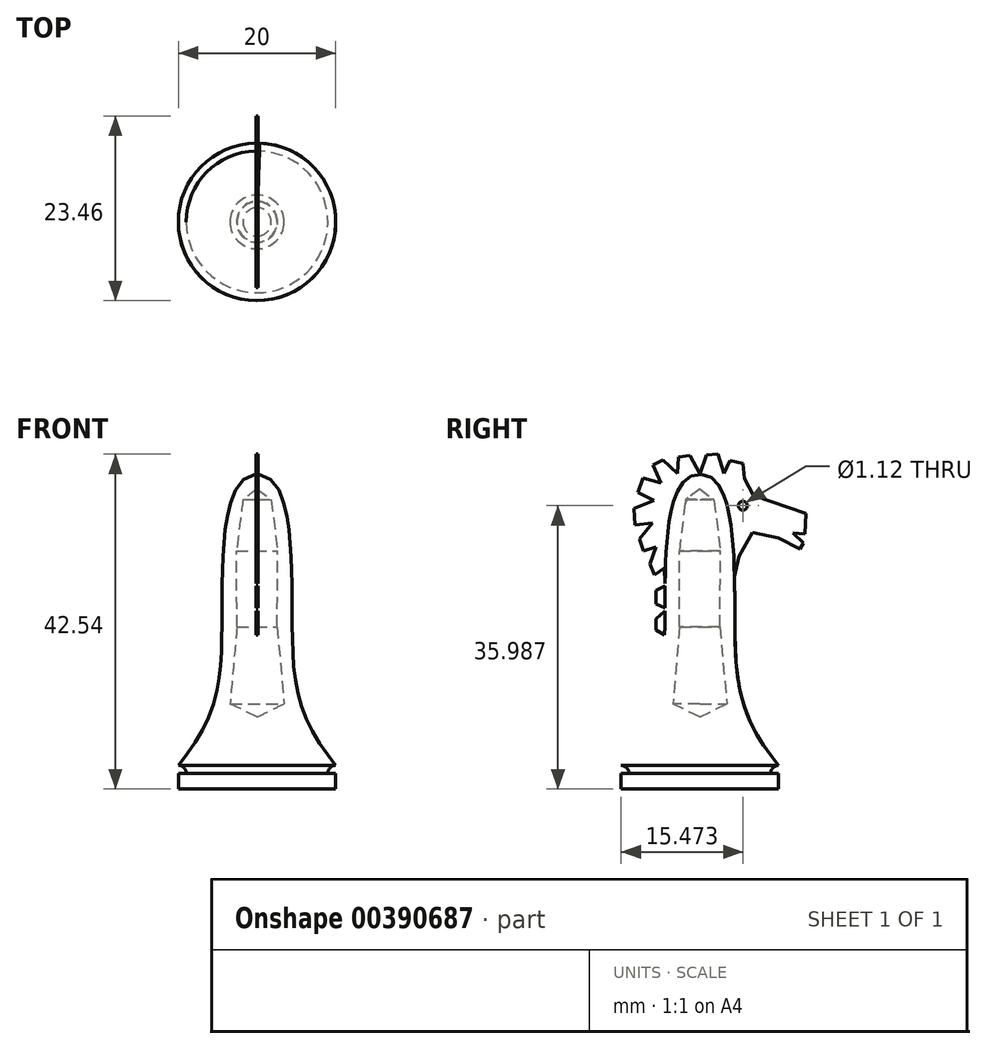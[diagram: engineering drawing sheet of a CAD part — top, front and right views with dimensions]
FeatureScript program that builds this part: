
annotation { "Feature Type Name" : "Feature", "Feature Type Description" : "" }
export const myFeature = defineFeature(function(context is Context, id is Id, definition is map)
    precondition{}
    {
        {
            assignVariable(context, id + "F0", {"name" : "r", "anyValue" : 1});
        }
        {
            var Q0;
            Q0=qCreatedBy(makeId("Front.planeOp"),FACE);
            var sketch = newSketch(context, id + "F1", { "sketchPlane" : qUnion([Q0])});
            skLineSegment(sketch, "E0", {"start": v(0, 0) * mm, "end": v(10, 0) * mm});
            skLineSegment(sketch, "E1", {"start": v(10, 0) * mm, "end": v(10, 2) * mm});
            skLineSegment(sketch, "E2", {"start": v(10, 2) * mm, "end": v(9, 2) * mm});
            skPoint(sketch, "E3.endSnap0", {"position": v(10, 1) * mm});
            skArc(sketch, "E4", {"start": v(9, 2) * mm, "mid": v(9.3, 2.7) * mm, "end": v(10, 3) * mm});
            skFitSpline(sketch, "E5", {"points": [v(10, 3) * mm, v(4.45, 21.57) * mm, v(0, 40) * mm], "startDerivative": vector(-30.93, 37.26) * mm, "endDerivative": vector(-27.95, 0.22) * mm});
            skLineSegment(sketch, "E6", {"start": v(0, 0) * mm, "end": v(0, 40) * mm});
            skLineSegment(sketch, "E7", {"start": v(0, 38.14) * mm, "end": v(1.8, 36.76) * mm});
            skLineSegment(sketch, "E8", {"start": v(1.8, 36.76) * mm, "end": v(2.62, 30.24) * mm});
            skLineSegment(sketch, "E9", {"start": v(2.62, 30.24) * mm, "end": v(2.55, 20.6) * mm});
            skLineSegment(sketch, "E10", {"start": v(2.55, 20.6) * mm, "end": v(3.43, 10.82) * mm});
            skLineSegment(sketch, "E11", {"start": v(3.43, 10.82) * mm, "end": v(0, 9.13) * mm});
            skSolve(sketch);
        }
        {
            var Q0;
            {var subQ0=sQuery(id+"F1.wireOp",EDGE,"E0");Q0=makeQuery(id+"F1.imprint","IMPRINT",FACE,{"disambiguationData":[TD([[makeQuery(id+"F1.imprint","IMPRINT",EDGE,{"derivedFrom":subQ0}),1.0]])]});}
            var Q1;
            {var subQ0=sQuery(id+"F1.wireOp",EDGE,"VEbEkys7-fiXa-1ozb-o1q4-QKgIsQ0NtL7G");Q1=makeQuery(id+"F1.imprint","IMPRINT",FACE,{"disambiguationData":[TD([[makeQuery(id+"F1.imprint","IMPRINT",EDGE,{"derivedFrom":subQ0}),-1.0]])]});}
            var Q2;
            {var subQ0=sQuery(id+"F1.wireOp",EDGE,"E6");var subQ3=sQuery(id+"F1.wireOp",EDGE,"UrGRKQzg-VSOa-ZteD-O5Gp-x69Zk8rxus1x");var subQ5=makeQuery(id+"F1.imprint","INTERSECT",VERTEX,{"derivedFrom":[subQ0,subQ3]});Q2=makeQuery(id+"F1.imprint","IMPRINT",FACE,{"disambiguationData":[TD([[makeQuery(id+"F1.imprint","IMPRINT",EDGE,{"disambiguationData":[TD([[subQ5,-1.0]])],"derivedFrom":subQ3}),1.0]])]});}
            var Q3;
            Q3=sQuery(id+"F1.wireOp",EDGE,"E6");
            revolve(context, id + "F2", {"entities" : qUnion([Q0, Q1, Q2]), "axis" : qUnion([Q3]), "revolveType" : RevolveType.FULL});
        }
        {
            var Q0;
            Q0=qCreatedBy(makeId("Right.planeOp"),FACE);
            var sketch = newSketch(context, id + "F3", { "sketchPlane" : qUnion([Q0])});
            skLineSegment(sketch, "E12", {"start": v(0, 40) * mm, "end": v(-1.25, 42.38) * mm});
            skLineSegment(sketch, "E13", {"start": v(-1.25, 42.38) * mm, "end": v(-2.73, 42.17) * mm});
            skLineSegment(sketch, "E14", {"start": v(-2.73, 42.17) * mm, "end": v(-2.82, 40.06) * mm});
            skLineSegment(sketch, "E15", {"start": v(-2.82, 40.06) * mm, "end": v(-4.66, 41.8) * mm});
            skLineSegment(sketch, "E16", {"start": v(-4.66, 41.8) * mm, "end": v(-5.94, 41.16) * mm});
            skLineSegment(sketch, "E17", {"start": v(-5.94, 41.16) * mm, "end": v(-4.93, 38.86) * mm});
            skLineSegment(sketch, "E18", {"start": v(-4.93, 38.86) * mm, "end": v(-7.23, 39.5) * mm});
            skLineSegment(sketch, "E19", {"start": v(-7.23, 39.5) * mm, "end": v(-7.88, 37.66) * mm});
            skLineSegment(sketch, "E20", {"start": v(-7.88, 37.66) * mm, "end": v(-5.85, 36.65) * mm});
            skLineSegment(sketch, "E21", {"start": v(-5.85, 36.65) * mm, "end": v(-8.34, 35.64) * mm});
            skLineSegment(sketch, "E22", {"start": v(-8.34, 35.64) * mm, "end": v(-8.24, 33.53) * mm});
            skLineSegment(sketch, "E23", {"start": v(-8.24, 33.53) * mm, "end": v(-6.04, 33.8) * mm});
            skLineSegment(sketch, "E24", {"start": v(-6.04, 33.8) * mm, "end": v(-7.7, 31.78) * mm});
            skLineSegment(sketch, "E25", {"start": v(-7.7, 31.78) * mm, "end": v(-7.14, 30.21) * mm});
            skLineSegment(sketch, "E26", {"start": v(-7.14, 30.21) * mm, "end": v(-5.58, 30.77) * mm});
            skLineSegment(sketch, "E27", {"start": v(-5.58, 30.77) * mm, "end": v(-6.31, 28.56) * mm});
            skLineSegment(sketch, "E28", {"start": v(-6.31, 28.56) * mm, "end": v(-5.76, 27.18) * mm});
            skLineSegment(sketch, "E29", {"start": v(-5.76, 27.18) * mm, "end": v(-4.47, 28.1) * mm});
            skLineSegment(sketch, "E30", {"start": v(-4.47, 28.1) * mm, "end": v(-4.4, 25.79) * mm});
            skLineSegment(sketch, "E31", {"start": v(-4.4, 25.79) * mm, "end": v(-5.58, 25.25) * mm});
            skLineSegment(sketch, "E32", {"start": v(-5.58, 25.25) * mm, "end": v(-5.58, 23.5) * mm});
            skLineSegment(sketch, "E33", {"start": v(-5.58, 23.5) * mm, "end": v(-4.2, 22.86) * mm});
            skLineSegment(sketch, "E34", {"start": v(-4.2, 22.86) * mm, "end": v(-5.58, 21.57) * mm});
            skLineSegment(sketch, "E35", {"start": v(-5.58, 21.57) * mm, "end": v(-5.58, 20.19) * mm});
            skLineSegment(sketch, "E36", {"start": v(-5.58, 20.19) * mm, "end": v(-4.16, 19.38) * mm});
            skLineSegment(sketch, "E37", {"start": v(0, 40) * mm, "end": v(0.86, 42.45) * mm});
            skLineSegment(sketch, "E38", {"start": v(0.86, 42.45) * mm, "end": v(2.33, 42.54) * mm});
            skLineSegment(sketch, "E39", {"start": v(2.33, 42.54) * mm, "end": v(3.07, 40.06) * mm});
            skLineSegment(sketch, "E40", {"start": v(3.07, 40.06) * mm, "end": v(3.8, 41.71) * mm});
            skLineSegment(sketch, "E41", {"start": v(3.8, 41.71) * mm, "end": v(5.46, 41.34) * mm});
            skLineSegment(sketch, "E42", {"start": v(5.46, 41.34) * mm, "end": v(5.64, 39.41) * mm});
            skLineSegment(sketch, "E43", {"start": v(5.64, 39.41) * mm, "end": v(6.84, 37.3) * mm});
            skLineSegment(sketch, "E44", {"start": v(6.84, 37.3) * mm, "end": v(13.46, 35) * mm});
            skLineSegment(sketch, "E45", {"start": v(13.46, 35) * mm, "end": v(13.37, 32.42) * mm});
            skLineSegment(sketch, "E46", {"start": v(13.37, 32.42) * mm, "end": v(11.8, 32.51) * mm});
            skLineSegment(sketch, "E47", {"start": v(11.8, 32.51) * mm, "end": v(13.19, 31.23) * mm});
            skLineSegment(sketch, "E48", {"start": v(13.19, 31.23) * mm, "end": v(12.73, 30.5) * mm});
            skLineSegment(sketch, "E49", {"start": v(12.73, 30.5) * mm, "end": v(9.97, 31.87) * mm});
            skLineSegment(sketch, "E50", {"start": v(9.97, 31.87) * mm, "end": v(6.66, 32.6) * mm});
            skLineSegment(sketch, "E51", {"start": v(6.66, 32.6) * mm, "end": v(5, 29.55) * mm});
            skLineSegment(sketch, "E52", {"start": v(5, 29.55) * mm, "end": v(3.68, 23.87) * mm});
            skLineSegment(sketch, "E53", {"start": v(4, 25.25) * mm, "end": v(2.76, 34.7) * mm});
            skLineSegment(sketch, "E54", {"start": v(2.76, 34.7) * mm, "end": v(0.99, 38.32) * mm});
            skLineSegment(sketch, "E55", {"start": v(0.99, 38.32) * mm, "end": v(-0.83, 38.32) * mm});
            skLineSegment(sketch, "E56", {"start": v(-0.83, 38.32) * mm, "end": v(-2.65, 34.7) * mm});
            skLineSegment(sketch, "E57", {"start": v(-2.65, 34.7) * mm, "end": v(-4.16, 19.38) * mm});
            skCircle(sketch, "E58", {"center": v(5.47, 35.99) * mm, "radius": 0.56 * mm});
            skSolve(sketch);
        }
        {
            var Q0;
            Q0 = qSketchRegion(id + "F3", true);
            extrude(context, id + "F4", {"entities" : qUnion([Q0]), "operationType" : NewBodyOperationType.ADD, "endBound" : BoundingType.SYMMETRIC, "depth" : (getVariable(context, 'r') * 0.3) * mm});
        }
    });
